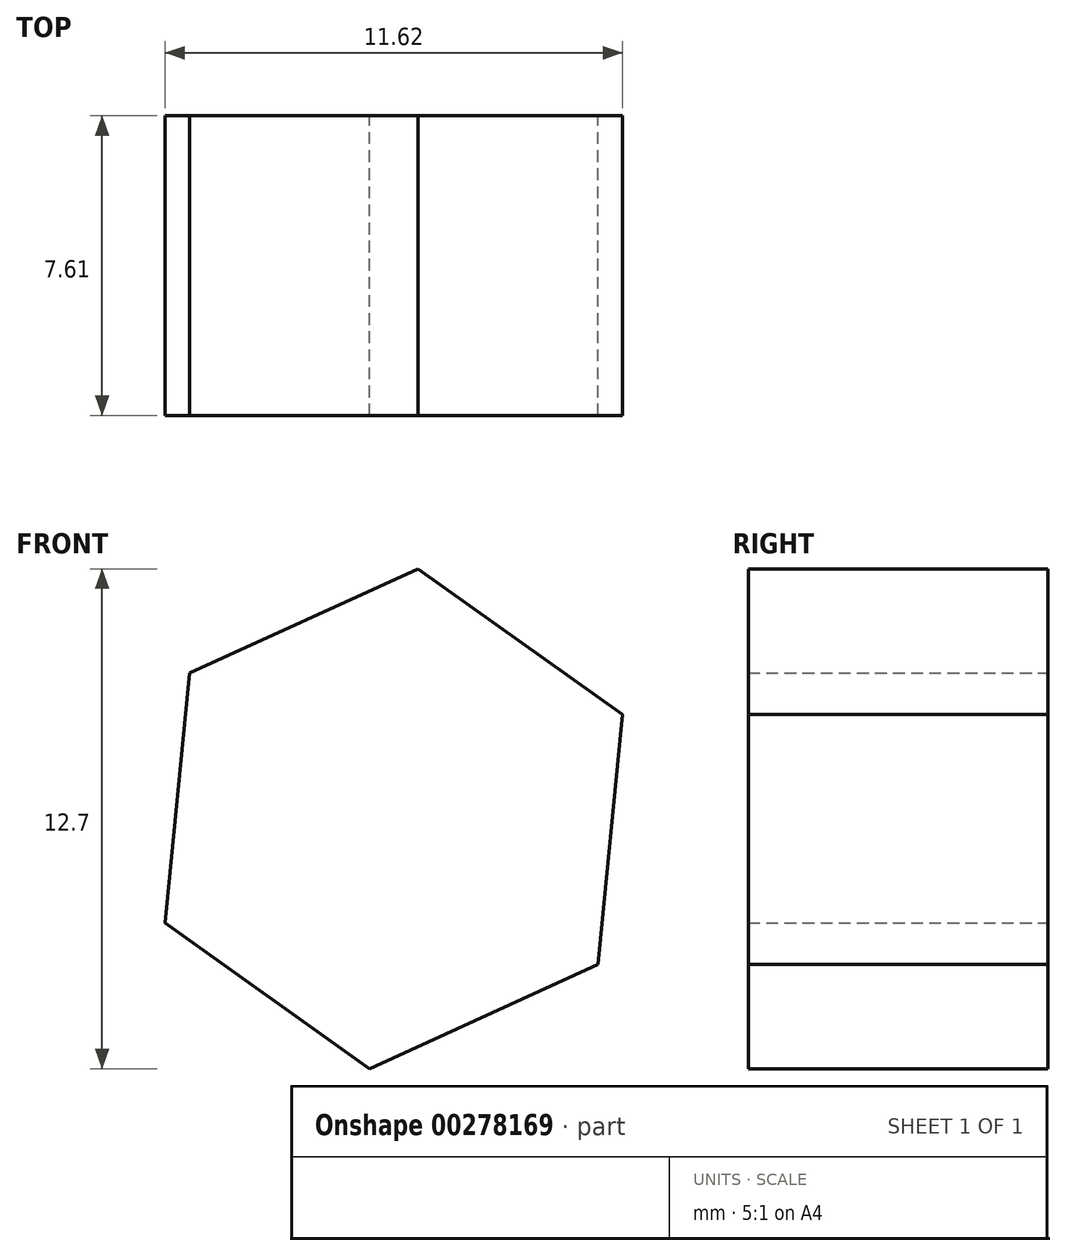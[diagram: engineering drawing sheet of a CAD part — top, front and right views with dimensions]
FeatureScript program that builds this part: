
annotation { "Feature Type Name" : "Feature", "Feature Type Description" : "" }
export const myFeature = defineFeature(function(context is Context, id is Id, definition is map)
    precondition{}
    {
        {
            var Q0;
            Q0=qCreatedBy(makeId("Front.planeOp"),FACE);
            var sketch = newSketch(context, id + "F1", { "sketchPlane" : qUnion([Q0])});
            skCircle(sketch, "E0.cCircle", {"center": v(0, 0) * mm, "radius": 6.38 * mm, "construction": true});
            skLineSegment(sketch, "E0.0", {"start": v(5.2, -3.7) * mm, "end": v(-0.61, -6.35) * mm});
            skLineSegment(sketch, "E0.1", {"start": v(-0.61, -6.35) * mm, "end": v(-5.8, -2.64) * mm});
            skLineSegment(sketch, "E0.2", {"start": v(-5.8, -2.64) * mm, "end": v(-5.2, 3.7) * mm});
            skLineSegment(sketch, "E0.3", {"start": v(-5.2, 3.7) * mm, "end": v(0.61, 6.35) * mm});
            skLineSegment(sketch, "E0.4", {"start": v(0.61, 6.35) * mm, "end": v(5.8, 2.64) * mm});
            skLineSegment(sketch, "E0.5", {"start": v(5.8, 2.64) * mm, "end": v(5.2, -3.7) * mm});
            skSolve(sketch);
        }
        {
            var Q0;
            Q0=makeQuery(id+"F1.imprint","IMPRINT",FACE,{"disambiguationData":[TD([[makeQuery(id+"F1.imprint","IMPRINT",EDGE,{"derivedFrom":sQuery(id+"F1.wireOp",EDGE,"E0.0")}),-1.0]])]});
            extrude(context, id + "F0", {"entities" : qUnion([Q0]), "depth" : 7.61 * mm});
        }
    });
